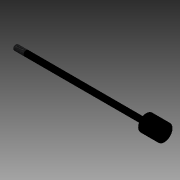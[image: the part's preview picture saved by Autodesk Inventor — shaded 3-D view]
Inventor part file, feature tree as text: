
AUTODESK INVENTOR PART (.ipt)
format: ipt  version: 2014 SP2 (Build 180246200, 246)  size: 133,632 bytes
history: native  units: in
note: dims shown in document units (in); Inventor stores cm internally (conversion verified against a paired STEP export)
features: other x70, revolve x3, sketch x3, thread x1
ambient origin geometry x8: Origin, YZ Plane, XZ Plane, XY Plane, X Axis, Y Axis, Z Axis, Center Point
bodies: Solid1 (feature_tree)
feature tree (77):
  revolve  "Revolution1"  Angle=360.0deg
  revolve  "Revolution2"  Angle=360.0deg
  thread  "Thread1"  [1 undecoded]
  revolve  "Revolution3"  [1 undecoded]
  other  "dia1_XY"
  other  "dia1_YZ"
  other  "dia1_ZX"
  other  "dia1_X"
  other  "dia1_Y"
  other  "dia1_Z"
  other  "dia1_Center"
  other  "dia12_XY"
  other  "dia12_YZ"
  other  "dia12_ZX"
  other  "dia12_X"
  other  "dia12_Y"
  other  "dia12_Z"
  other  "dia12_Center"
  other  "dia2_XY"
  other  "dia2_YZ"
  other  "dia2_ZX"
  other  "dia2_X"
  other  "dia2_Y"
  other  "dia2_Z"
  other  "dia2_Center"
  other  "dia22_XY"
  other  "dia22_YZ"
  other  "dia22_ZX"
  other  "dia22_X"
  other  "dia22_Y"
  other  "dia22_Z"
  other  "dia22_Center"
  other  "rl1_XY"
  other  "rl1_YZ"
  other  "rl1_ZX"
  other  "rl1_X"
  other  "rl1_Y"
  other  "rl1_Z"
  other  "rl1_Center"
  other  "rl2_XY"
  other  "rl2_YZ"
  other  "rl2_ZX"
  other  "rl2_X"
  other  "rl2_Y"
  other  "rl2_Z"
  other  "rl2_Center"
  other  "rod_cp_XY"
  other  "rod_cp_YZ"
  other  "rod_cp_ZX"
  other  "rod_cp_X"
  other  "rod_cp_Y"
  other  "rod_cp_Z"
  other  "rod_cp_Center"
  other  "thd1_XY"
  other  "thd1_YZ"
  other  "thd1_ZX"
  other  "thd1_X"
  other  "thd1_Y"
  other  "thd1_Z"
  other  "thd1_Center"
  other  "thd2_XY"
  other  "thd2_YZ"
  other  "thd2_ZX"
  other  "thd2_X"
  other  "thd2_Y"
  other  "thd2_Z"
  other  "thd2_Center"
  other  "to_rod_clevis_XY"
  other  "to_rod_clevis_YZ"
  other  "to_rod_clevis_ZX"
  other  "to_rod_clevis_X"
  other  "to_rod_clevis_Y"
  other  "to_rod_clevis_Z"
  other  "to_rod_clevis_Center"
  sketch  "Sketch_1"  dims[d0=360.0deg d1=360.0deg]
  sketch  "Sketch_3"  dims[d2=0.4787in d3=0.0in d4=360.0deg]
  sketch  "Sketch_30"  dims[d5=0.0in d6=0.0in d7=0.0in d8=0.0in d9=0.0in]
note: 2 required parameter values undecoded (feature->parameter linkage not recoverable at this tier; creation-order binding heuristic only, values carry confidence <= 0.55)
